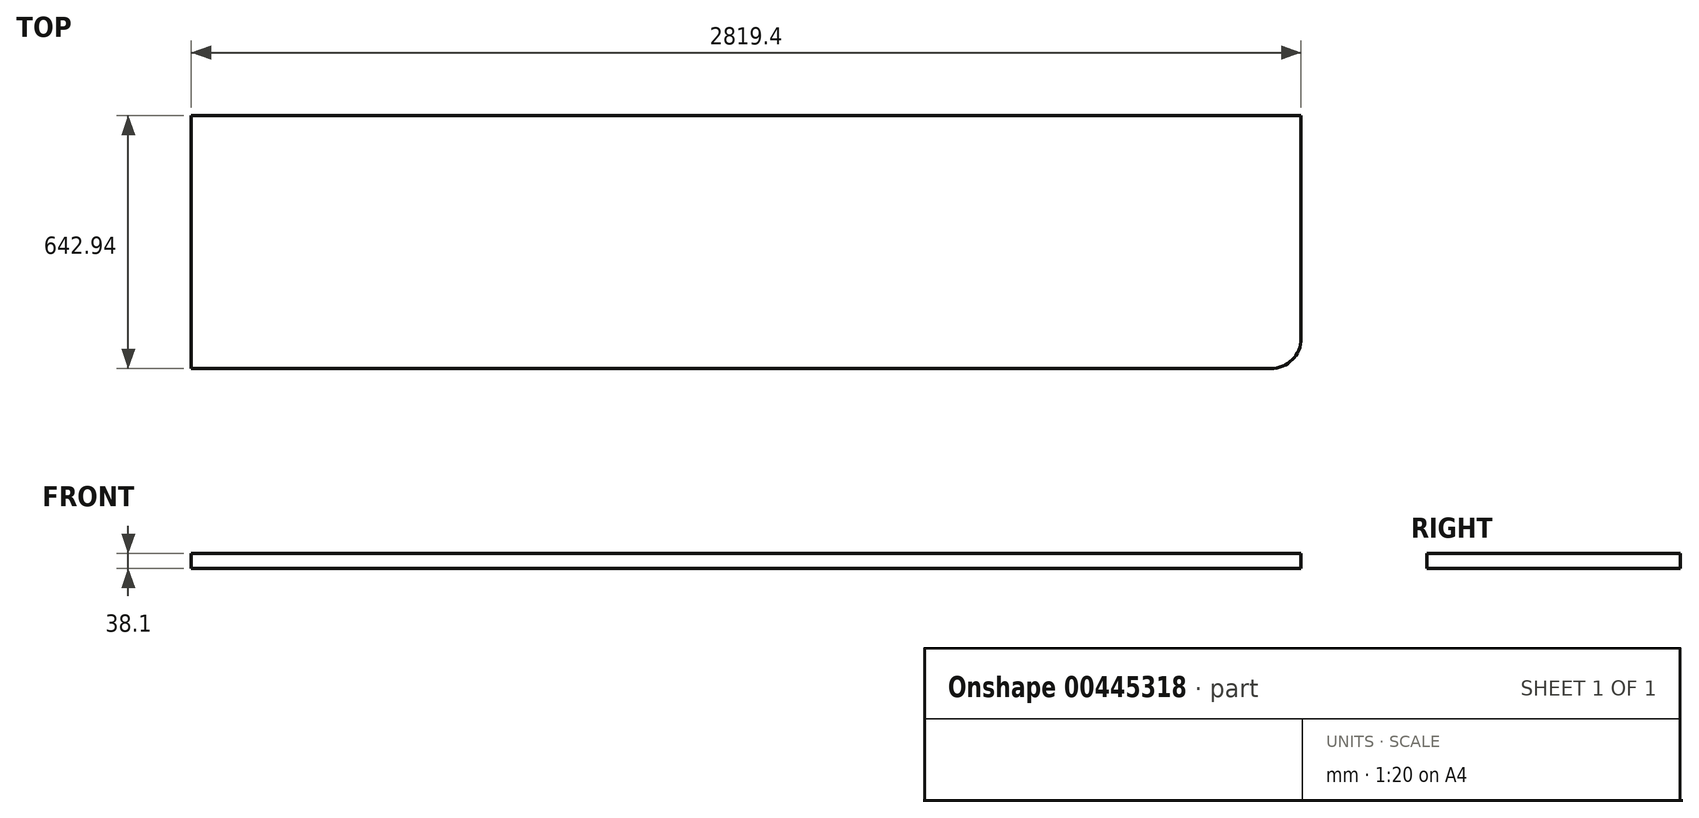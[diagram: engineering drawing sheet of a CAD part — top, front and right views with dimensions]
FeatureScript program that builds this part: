
annotation { "Feature Type Name" : "Feature", "Feature Type Description" : "" }
export const myFeature = defineFeature(function(context is Context, id is Id, definition is map)
    precondition{}
    {
        {
            var Q0;
            Q0=qCreatedBy(makeId("Top.planeOp"),FACE);
            var sketch = newSketch(context, id + "F0", { "sketchPlane" : qUnion([Q0])});
            skLineSegment(sketch, "E0.bottom", {"start": v(0, 0) * mm, "end": v(2819.4, 0) * mm});
            skLineSegment(sketch, "E0.top", {"start": v(0, -642.94) * mm, "end": v(2819.4, -642.94) * mm});
            skLineSegment(sketch, "E0.left", {"start": v(0, 0) * mm, "end": v(0, -642.94) * mm});
            skLineSegment(sketch, "E0.right", {"start": v(2819.4, 0) * mm, "end": v(2819.4, -642.94) * mm});
            skSolve(sketch);
        }
        {
            var Q0;
            Q0=makeQuery(id+"F0.imprint","IMPRINT",FACE,{"disambiguationData":[TD([[makeQuery(id+"F0.imprint","IMPRINT",EDGE,{"derivedFrom":sQuery(id+"F0.wireOp",EDGE,"E0.bottom")}),-1.0]])]});
            extrude(context, id + "F1", {"entities" : qUnion([Q0]), "depth" : 38.1 * mm});
        }
        {
            var Q0;
            Q0=makeQuery(id+"F1.opExtrude","SWEPT_EDGE",EDGE,{"disambiguationData":[OSD([sQuery(id+"F0.wireOp",EDGE,"E0.top"),sQuery(id+"F0.wireOp",EDGE,"E0.right")])]});
            fillet(context, id + "F2", {"entities" : qUnion([Q0]), "radius" : 76.2 * mm, "tangentPropagation" : true, "allowEdgeOverflow" : false});
        }
    });
